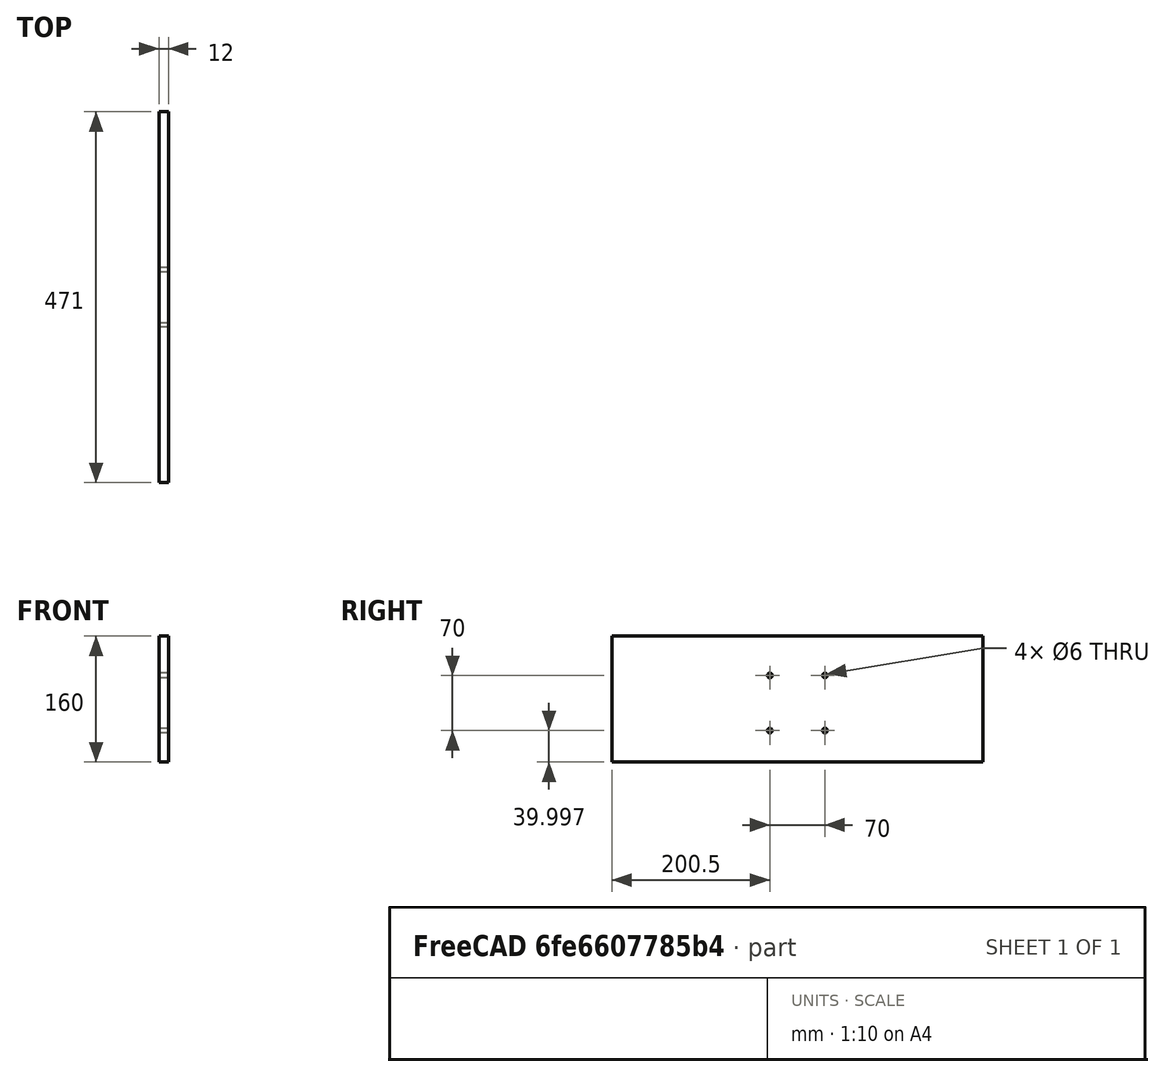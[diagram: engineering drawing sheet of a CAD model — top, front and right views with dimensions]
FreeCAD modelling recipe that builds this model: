
FCSTD DOCUMENT  (FreeCAD 0.19R24276 (Git))
Label: 8030_Box_Frame_Back
License: All rights reserved
LicenseURL: http://en.wikipedia.org/wiki/All_rights_reserved
objects: Spreadsheet::Sheet×1, Sketcher::SketchObject×1, PartDesign::Pad×1, PartDesign::Body×1
note: 4 computed .brp shape members not serialized (recipe doc carries the construction recipe); baked Part::Feature solids carry a one-line shape summary decoded from their .brp

FEATURE [Spreadsheet::Sheet] Spreadsheet
  cells = B2=FRAME BASE; B3=Z=; C3(T)=12; D3=.T; E3=Thichness; B4=Y=; C4(Width)==495 - C3 - C3; D4=.W; E4=Width; B5=X=; C5(Height)=160; D5=.D; E5=Height$
FEATURE [Sketcher::SketchObject] Sketch
  FullyConstrained = false
  MapMode = 5
  Placement = pos=(0,0,0) rot=(0.57735,0.57735,0.57735;2.0944rad)
  Support = -> [YZ_Plane]
  expr: Constraints[14] = Spreadsheet.Height
  expr: Constraints[12] = Spreadsheet.Width
  sketch-geometry (14):
    g0: LineSegment StartX=-235.5 StartY=118.337 StartZ=0 EndX=235.5 EndY=118.337 EndZ=0
    g1: LineSegment StartX=235.5 StartY=118.337 StartZ=0 EndX=235.5 EndY=-41.6625 EndZ=0
    g2: LineSegment StartX=235.5 StartY=-41.6625 StartZ=0 EndX=-235.5 EndY=-41.6625 EndZ=0
    g3: LineSegment StartX=-235.5 StartY=-41.6625 StartZ=0 EndX=-235.5 EndY=118.337 EndZ=0
    g4: LineSegment StartX=-235.5 StartY=-41.6625 StartZ=0 EndX=0 EndY=54.6665 EndZ=0
    g5: LineSegment StartX=0 StartY=54.6665 StartZ=0 EndX=235.5 EndY=-41.6625 EndZ=0
    g6: LineSegment StartX=-35 StartY=68.3375 StartZ=0 EndX=0 EndY=68.3375 EndZ=0
    g7: LineSegment StartX=-35 StartY=-1.66252 StartZ=0 EndX=-35 EndY=68.3375 EndZ=0
    g8: LineSegment StartX=35 StartY=-1.66252 StartZ=0 EndX=35 EndY=68.3375 EndZ=0
    g9: LineSegment StartX=35 StartY=68.3375 StartZ=0 EndX=0 EndY=68.3375 EndZ=0
    g10: Circle CenterX=35 CenterY=68.3375 CenterZ=0 NormalX=0 NormalY=0 NormalZ=1 AngleXU=0 Radius=3
    g11: Circle CenterX=35 CenterY=-1.66252 CenterZ=0 NormalX=0 NormalY=0 NormalZ=1 AngleXU=0 Radius=3
    g12: Circle CenterX=-35 CenterY=-1.66252 CenterZ=0 NormalX=0 NormalY=0 NormalZ=1 AngleXU=0 Radius=3
    g13: Circle CenterX=-35 CenterY=68.3375 CenterZ=0 NormalX=0 NormalY=0 NormalZ=1 AngleXU=0 Radius=3
  constraints (36):
    c: Coincident(g0,g1)
    c: Coincident(g1,g2)
    c: Coincident(g2,g3)
    c: Coincident(g3,g0)
    c: Horizontal(g0)
    c: Horizontal(g2)
    c: Vertical(g1)
    c: Vertical(g3)
    c: Coincident(g4,g2)
    c: PointOnObject(g4,g-2)
    c: Coincident(g5,g4)
    c: Coincident(g5,g1)
    c: DistanceX(g0,g0) = 471
    c: Equal(g5,g4)
    c: DistanceY(g3,g3) = 160
    c: Coincident(g7,g6)
    c: Horizontal(g6)
    c: Vertical(g7)
    c: Coincident(g8,g9)
    c: Horizontal(g9)
    c: Vertical(g8)
    c: Coincident(g9,g6)
    c: Equal(g9,g6)
    c: PointOnObject(g6,g-2)
    c: DistanceX(g6,g8) = 70
    c: DistanceY(g8,g8) = 70
    c: Coincident(g10,g8)
    c: Coincident(g11,g8)
    c: Coincident(g12,g7)
    c: Coincident(g13,g6)
    c: Equal(g13,g12)
    c: Equal(g12,g11)
    c: Equal(g11,g10)
    c: Diameter(g10) = 6
    c: Equal(g7,g8)
    c: DistanceY(g1,g11) = 40
FEATURE [PartDesign::Pad] Pad
  Direction = (1,1,1)
  Length = 12
  Length2 = 100
  Placement = pos=(0,0,0) rot=(0.57735,0.57735,0.57735;2.0944rad)
  Profile = -> Sketch
  Type = 0
FEATURE [PartDesign::Body] Body
  Group = -> [Sketch,Pad]
  Origin = -> Origin
  Tip = -> Pad
